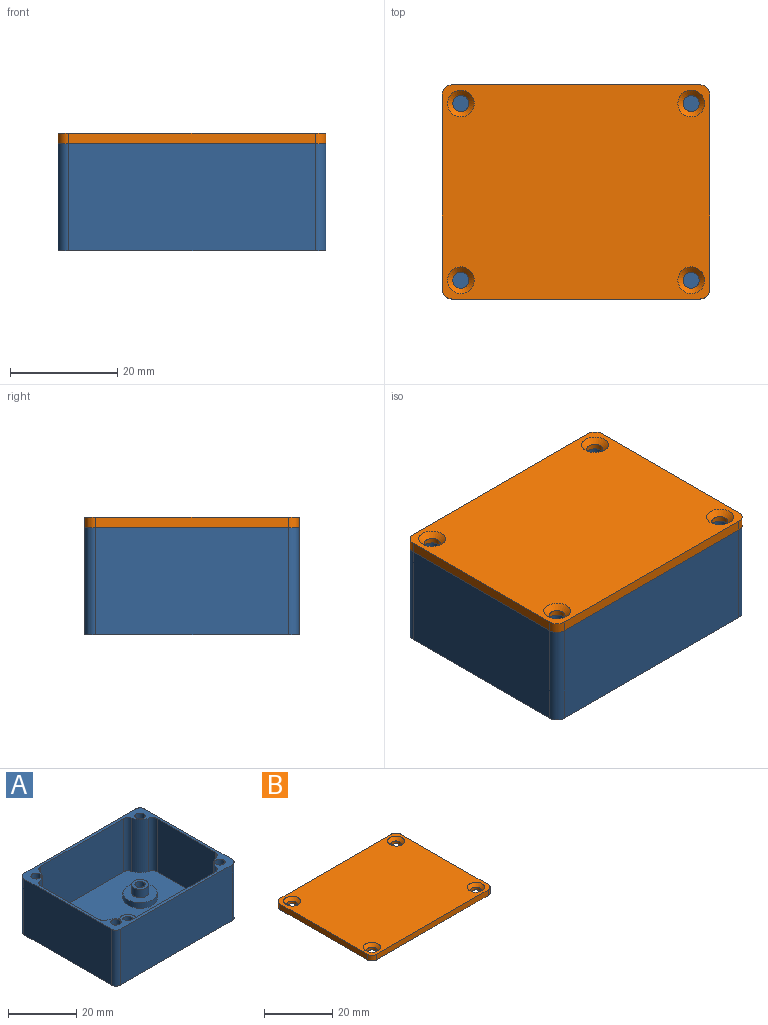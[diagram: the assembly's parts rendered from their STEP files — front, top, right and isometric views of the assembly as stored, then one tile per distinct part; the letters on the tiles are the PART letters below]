
ASSEMBLY  parts=2 mates=1
PART A: 59 faces, bbox 50x40x20 mm
  f0: plane 48x38mm, normal (0,0,1), area 1574.5mm2, adj f1,f2,f3,f4,f20,f25,f47,f48
  f1: plane 34x19mm, normal (0,1,0), area 646mm2, adj f0,f5,f47,f49
  f2: plane 24x19mm, normal (-1,0,0), area 456mm2, adj f0,f5,f50,f51
  f3: plane 34x19mm, normal (0,-1,0), area 646mm2, adj f0,f5,f52,f53
  f4: plane 24x19mm, normal (1,0,0), area 456mm2, adj f0,f5,f48,f54
  f5: plane 50x40mm, normal (0,0,1), area 236.8mm2, adj f1,f2,f3,f4,f6,f7,f8,f9
  f6: plane 46x20mm, normal (0,1,0), area 920mm2, adj f5,f10,f43,f46
  f7: plane 36x20mm, normal (-1,0,0), area 720mm2, adj f5,f10,f43,f44
  f8: plane 46x20mm, normal (0,-1,0), area 920mm2, adj f5,f10,f44,f45
  f9: plane 36x20mm, normal (1,0,0), area 720mm2, adj f5,f10,f45,f46
  f10: plane 50x40mm, normal (0,0,-1), area 1949.8mm2, adj f6,f7,f8,f9,f29,f30,f31,f32
  f11: cylinder r=1.5mm len=10mm, axis (0,0,1), area 94.2mm2, adj f5,f12
  f12: plane 3x3mm, normal (0,0,1), area 7.1mm2, adj f11
  f13: cylinder r=1.5mm len=10mm, axis (0,0,1), area 94.2mm2, adj f5,f14
  f14: plane 3x3mm, normal (0,0,1), area 7.1mm2, adj f13
  f15: cylinder r=1.5mm len=10mm, axis (0,0,1), area 94.2mm2, adj f5,f16
  f16: plane 3x3mm, normal (0,0,1), area 7.1mm2, adj f15
  f17: cylinder r=1.5mm len=10mm, axis (0,0,1), area 94.2mm2, adj f5,f18
  f18: plane 3x3mm, normal (0,0,1), area 7.1mm2, adj f17
  f19: plane 10x10mm, normal (0,0,1), area 58.9mm2, adj f20,f23
  f20: cylinder r=5mm len=10mm, axis (0,0,-1), area 62.8mm2, adj f0,f19
  f21: cylinder r=1.5mm len=4mm, axis (0,0,-1), area 37.7mm2, adj f22,f42
  f22: plane 5x5mm, normal (0,0,1), area 12.6mm2, adj f21,f23
  f23: cylinder r=2.5mm len=5mm, axis (0,0,-1), area 47.1mm2, adj f19,f22
  f24: plane 10x10mm, normal (0,0,1), area 58.9mm2, adj f25,f28
  f25: cylinder r=5mm len=10mm, axis (0,0,-1), area 62.8mm2, adj f0,f24
  f26: cylinder r=1.5mm len=4mm, axis (0,0,-1), area 37.7mm2, adj f27,f35
  f27: plane 5x5mm, normal (0,0,1), area 12.6mm2, adj f26,f28
  f28: cylinder r=2.5mm len=5mm, axis (0,0,-1), area 47.1mm2, adj f24,f27
  f29: plane 2.96x2mm, normal (-0.15,-0.99,0), area 6mm2, adj f10,f30,f34,f35
  f30: plane 2.8x2mm, normal (-0.93,-0.36,0), area 6mm2, adj f10,f29,f31,f35
  f31: plane 2.34x2mm, normal (-0.78,0.63,0), area 6mm2, adj f10,f30,f32,f35
  f32: plane 2.96x2mm, normal (0.15,0.99,0), area 6mm2, adj f10,f31,f33,f35
  f33: plane 2.8x2mm, normal (0.93,0.36,0), area 6mm2, adj f10,f32,f34,f35
  f34: plane 2.34x2mm, normal (0.78,-0.63,0), area 6mm2, adj f10,f29,f33,f35
  f35: plane 5.93x5.6mm, normal (0,0,-1), area 16.3mm2, adj f26,f29,f30,f31,f32,f33,f34
  f36: plane 2.24x2mm, normal (-0.67,-0.75,0), area 6mm2, adj f10,f37,f41,f42
  f37: plane 2.94x2mm, normal (-0.98,0.2,0), area 6mm2, adj f10,f36,f38,f42
  f38: plane 2.85x2mm, normal (-0.31,0.95,0), area 6mm2, adj f10,f37,f39,f42
  f39: plane 2.24x2mm, normal (0.67,0.75,0), area 6mm2, adj f10,f38,f40,f42
  f40: plane 2.94x2mm, normal (0.98,-0.2,0), area 6mm2, adj f10,f39,f41,f42
  f41: plane 2.85x2mm, normal (0.31,-0.95,0), area 6mm2, adj f10,f36,f40,f42
  f42: plane 5.88x5.7mm, normal (0,0,-1), area 16.3mm2, adj f21,f36,f37,f38,f39,f40,f41
  f43: cylinder r=2mm len=20mm, axis (0,0,1), area 62.8mm2, adj f5,f6,f7,f10
  f44: cylinder r=2mm len=20mm, axis (0,0,-1), area 62.8mm2, adj f5,f7,f8,f10
  f45: cylinder r=2mm len=20mm, axis (0,0,1), area 62.8mm2, adj f5,f8,f9,f10
  f46: cylinder r=2mm len=20mm, axis (0,0,-1), area 62.8mm2, adj f5,f6,f9,f10
  f47: cylinder r=2mm len=19mm, axis (0,0,-1), area 50mm2, adj f0,f1,f5,f55
  f48: cylinder r=2mm len=19mm, axis (0,0,1), area 50mm2, adj f0,f4,f5,f55
  f49: cylinder r=2mm len=19mm, axis (0,0,1), area 50mm2, adj f0,f1,f5,f56
  f50: cylinder r=2mm len=19mm, axis (0,0,1), area 50mm2, adj f0,f2,f5,f56
  f51: cylinder r=2mm len=19mm, axis (0,0,-1), area 50mm2, adj f0,f2,f5,f57
  f52: cylinder r=2mm len=19mm, axis (0,0,1), area 50mm2, adj f0,f3,f5,f57
  f53: cylinder r=2mm len=19mm, axis (0,0,-1), area 50mm2, adj f0,f3,f5,f58
  f54: cylinder r=2mm len=19mm, axis (0,0,-1), area 50mm2, adj f0,f4,f5,f58
  f55: cylinder r=5mm len=19mm, axis (0,0,-1), area 100.6mm2, adj f0,f5,f47,f48
  f56: cylinder r=5mm len=19mm, axis (0,0,-1), area 100.6mm2, adj f0,f5,f49,f50
  f57: cylinder r=5mm len=19mm, axis (0,0,-1), area 100.6mm2, adj f0,f5,f51,f52
  f58: cylinder r=5mm len=19mm, axis (0,0,-1), area 100.6mm2, adj f0,f5,f53,f54
PART B: 18 faces, bbox 50x40x2 mm
  f0: plane 46x2mm, normal (0,1,0), area 92mm2, adj f4,f5,f14,f17
  f1: plane 36x2mm, normal (-1,0,0), area 72mm2, adj f4,f5,f14,f15
  f2: plane 46x2mm, normal (0,-1,0), area 92mm2, adj f4,f5,f15,f16
  f3: plane 36x2mm, normal (1,0,0), area 72mm2, adj f4,f5,f16,f17
  f4: plane 50x40mm, normal (0,0,1), area 1918mm2, adj f0,f1,f2,f3,f10,f11,f12,f13
  f5: plane 50x40mm, normal (0,0,-1), area 1968.3mm2, adj f0,f1,f2,f3,f6,f7,f8,f9
  f6: cylinder r=1.5mm len=3mm, axis (0,0,1), area 9.4mm2, adj f5,f13
  f7: cylinder r=1.5mm len=3mm, axis (0,0,1), area 9.4mm2, adj f5,f12
  f8: cylinder r=1.5mm len=3mm, axis (0,0,1), area 9.4mm2, adj f5,f11
  f9: cylinder r=1.5mm len=3mm, axis (0,0,1), area 9.4mm2, adj f5,f10
  f10: cone r=1.5mm half-angle=45deg, axis (0,0,1), area 17.8mm2, adj f4,f9
  f11: cone r=1.5mm half-angle=45deg, axis (0,0,1), area 17.8mm2, adj f4,f8
  f12: cone r=1.5mm half-angle=45deg, axis (0,0,1), area 17.8mm2, adj f4,f7
  f13: cone r=1.5mm half-angle=45deg, axis (0,0,1), area 17.8mm2, adj f4,f6
  f14: cylinder r=2mm len=2mm, axis (0,0,1), area 6.3mm2, adj f0,f1,f4,f5
  f15: cylinder r=2mm len=2mm, axis (0,0,-1), area 6.3mm2, adj f1,f2,f4,f5
  f16: cylinder r=2mm len=2mm, axis (0,0,1), area 6.3mm2, adj f2,f3,f4,f5
  f17: cylinder r=2mm len=2mm, axis (0,0,-1), area 6.3mm2, adj f0,f3,f4,f5
PLACE A t=(-37.75,-32,15.85)mm fixed
PLACE B t=(-112.34,-33.97,35.85)mm
MATE slider A.f15 <-> B.f8  axis (0,0,1) through (-52.05,-6.63,35.85)mm
